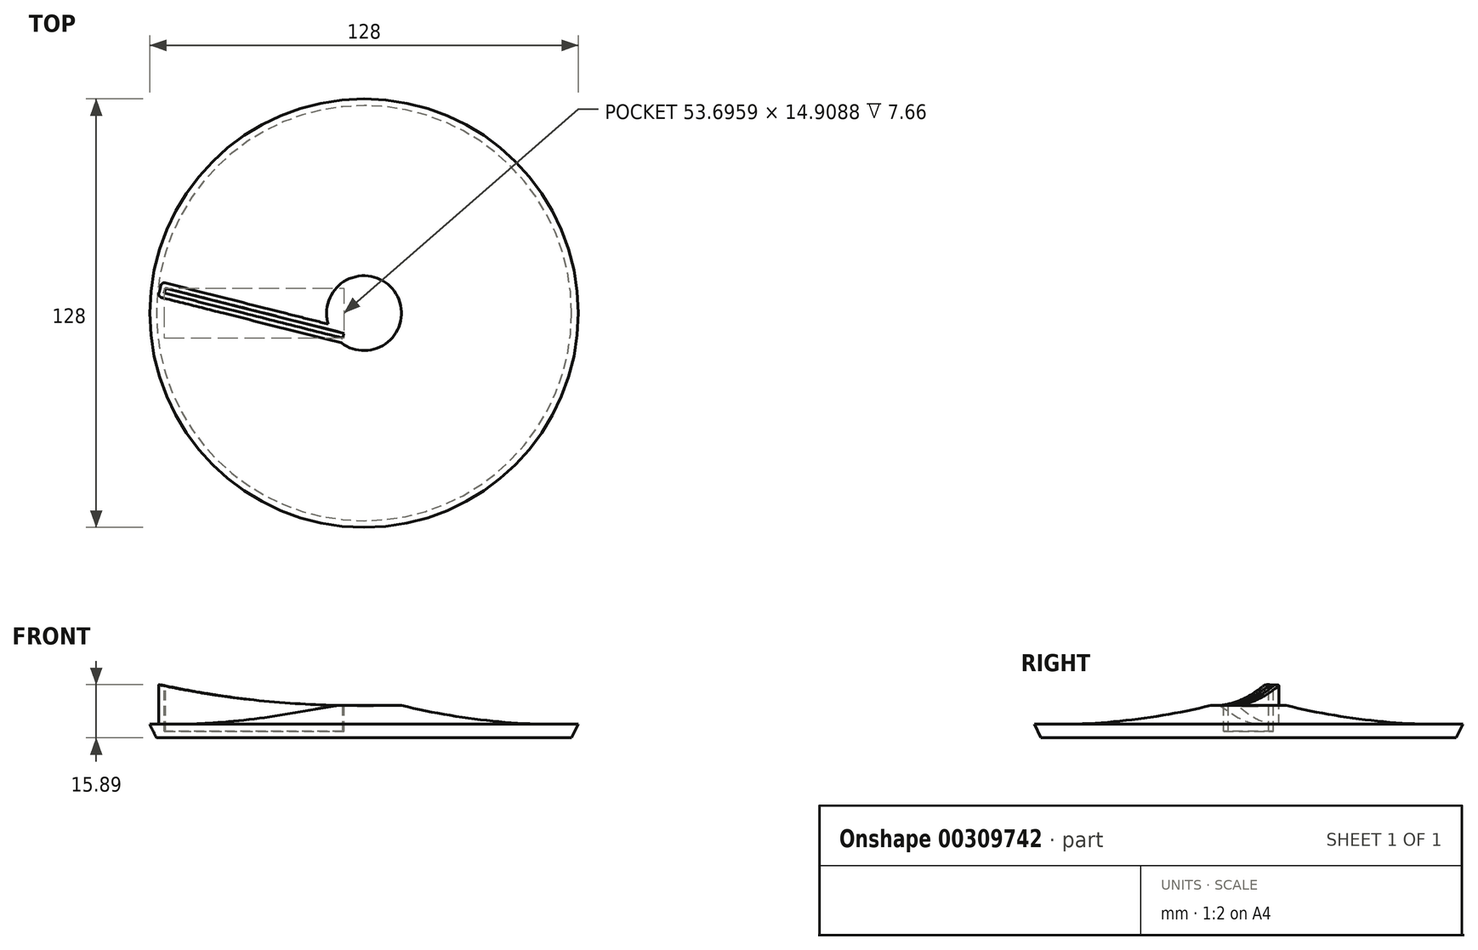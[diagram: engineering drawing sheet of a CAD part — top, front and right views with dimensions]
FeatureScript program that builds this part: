
annotation { "Feature Type Name" : "Feature", "Feature Type Description" : "" }
export const myFeature = defineFeature(function(context is Context, id is Id, definition is map)
    precondition{}
    {
        {
            var Q0;
            Q0=qCreatedBy(makeId("Front.planeOp"),FACE);
            var sketch = newSketch(context, id + "F0", { "sketchPlane" : qUnion([Q0])});
            skLineSegment(sketch, "E0", {"start": v(-62, 0) * mm, "end": v(-64, 4.07) * mm});
            skLineSegment(sketch, "E1", {"start": v(0, 0) * mm, "end": v(-62, 0) * mm});
            skArc(sketch, "E2", {"start": v(-64, 4.07) * mm, "mid": v(-36.8, 5.2) * mm, "end": v(-10, 10) * mm});
            skArc(sketch, "E3", {"start": v(-300, 309.5) * mm, "mid": v(-212.13, 97.37) * mm, "end": v(0, 9.5) * mm});
            skLineSegment(sketch, "E4", {"start": v(0, 0) * mm, "end": v(0, 309.5) * mm});
            skLineSegment(sketch, "E5", {"start": v(-300, 309.5) * mm, "end": v(0, 309.5) * mm});
            skLineSegment(sketch, "E6", {"start": v(-10, 10) * mm, "end": v(0, 10) * mm});
            skSolve(sketch);
        }
        {
            var Q0;
            Q0=qCreatedBy(makeId("Top.planeOp"),FACE);
            cPlane(context, id + "F1", {"entities" : qUnion([Q0]), "cplaneType" : CPlaneType.OFFSET, "offset" : 20 * mm, "width" : 150 * mm, "height" : 150 * mm});
        }
        {
            var Q0;
            Q0=qCreatedBy(id+"F1.planeOp",FACE);
            var sketch = newSketch(context, id + "F2", { "sketchPlane" : qUnion([Q0])});
            skLineSegment(sketch, "E7", {"start": v(-59.7, 6) * mm, "end": v(-59.33, 7.45) * mm});
            skLineSegment(sketch, "E8", {"start": v(-59.33, 7.45) * mm, "end": v(-6, -6) * mm});
            skLineSegment(sketch, "E9", {"start": v(-6, -6) * mm, "end": v(-6.37, -7.45) * mm});
            skLineSegment(sketch, "E10", {"start": v(-6.37, -7.45) * mm, "end": v(-59.7, 6) * mm});
            skLineSegment(sketch, "E11", {"start": v(-60.42, 9.28) * mm, "end": v(-4.18, -4.91) * mm});
            skLineSegment(sketch, "E12", {"start": v(-4.18, -4.91) * mm, "end": v(-5.28, -9.28) * mm});
            skLineSegment(sketch, "E13", {"start": v(-5.28, -9.28) * mm, "end": v(-61.52, 4.91) * mm});
            skLineSegment(sketch, "E14", {"start": v(-61.52, 4.91) * mm, "end": v(-60.42, 9.28) * mm});
            skSolve(sketch);
        }
        {
            var Q0;
            {var subQ1=sQuery(id+"F0.wireOp",EDGE,"E0");Q0=makeQuery(id+"F0.imprint","IMPRINT",FACE,{"disambiguationData":[TD([[makeQuery(id+"F0.imprint","IMPRINT",EDGE,{"derivedFrom":subQ1}),-1.0]])]});}
            var Q1;
            {var subQ0=sQuery(id+"F0.wireOp",EDGE,"Ql11Jk5t-lFoq-PQFx-toqf-jOswFTIF0uUF");Q1=makeQuery(id+"F0.imprint","IMPRINT",FACE,{"disambiguationData":[TD([[makeQuery(id+"F0.imprint","IMPRINT",EDGE,{"derivedFrom":subQ0}),1.0]])]});}
            var Q2;
            Q2=sQuery(id+"F0.wireOp",EDGE,"E4");
            revolve(context, id + "F3", {"entities" : qUnion([Q0, Q1]), "axis" : qUnion([Q2]), "revolveType" : RevolveType.FULL});
        }
        {
            var Q0;
            Q0=makeQuery(id+"F2.imprint","IMPRINT",FACE,{"disambiguationData":[TD([[makeQuery(id+"F2.imprint","IMPRINT",EDGE,{"derivedFrom":sQuery(id+"F2.wireOp",EDGE,"E7")}),1.0]])]});
            extrude(context, id + "F4", {"entities" : qUnion([Q0]), "operationType" : NewBodyOperationType.ADD, "oppositeDirection" : true, "depth" : 17 * mm});
        }
        {
            var Q0;
            Q0=makeQuery(id+"F2.imprint","IMPRINT",FACE,{"disambiguationData":[TD([[makeQuery(id+"F2.imprint","IMPRINT",EDGE,{"derivedFrom":sQuery(id+"F2.wireOp",EDGE,"E7")}),-1.0]])]});
            extrude(context, id + "F5", {"entities" : qUnion([Q0]), "operationType" : NewBodyOperationType.REMOVE, "oppositeDirection" : true, "depth" : 18 * mm});
        }
        {
            var Q0;
            {var subQ0=sQuery(id+"F0.wireOp",EDGE,"E5");Q0=makeQuery(id+"F0.imprint","IMPRINT",FACE,{"disambiguationData":[TD([[makeQuery(id+"F0.imprint","IMPRINT",EDGE,{"derivedFrom":subQ0}),-1.0]])]});}
            var Q1;
            {var subQ0=sQuery(id+"F0.wireOp",EDGE,"E6");Q1=makeQuery(id+"F0.imprint","IMPRINT",FACE,{"disambiguationData":[TD([[makeQuery(id+"F0.imprint","IMPRINT",EDGE,{"derivedFrom":subQ0}),-1.0]])]});}
            var Q2;
            Q2=sQuery(id+"F0.wireOp",EDGE,"E4");
            revolve(context, id + "F6", {"operationType" : NewBodyOperationType.REMOVE, "entities" : qUnion([Q0, Q1]), "axis" : qUnion([Q2]), "revolveType" : RevolveType.FULL, "oppositeDirection" : true});
        }
        {
            var Q0;
            Q0=makeQuery(id+"F4.opExtrude","SWEPT_EDGE",EDGE,{"disambiguationData":[OSD([sQuery(id+"F2.wireOp",EDGE,"E13"),sQuery(id+"F2.wireOp",EDGE,"E14")])]});
            var Q1;
            Q1=makeQuery(id+"F4.opExtrude","SWEPT_EDGE",EDGE,{"disambiguationData":[OSD([sQuery(id+"F2.wireOp",EDGE,"E11"),sQuery(id+"F2.wireOp",EDGE,"E14")])]});
            fillet(context, id + "F7", {"entities" : qUnion([Q0, Q1]), "radius" : 1 * mm, "tangentPropagation" : true, "allowEdgeOverflow" : false});
        }
    });
